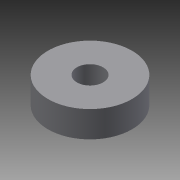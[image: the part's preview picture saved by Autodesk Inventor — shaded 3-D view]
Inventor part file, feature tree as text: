
AUTODESK INVENTOR PART (.ipt)
format: ipt  version: 2013 (Build 170138000, 138)  size: 72,704 bytes
history: native  units: mm
features: extrude x1, sketch x1
ambient origin geometry x8: Origin, YZ Plane, XZ Plane, XY Plane, X Axis, Y Axis, Z Axis, Center Point
bodies: Solid1 (feature_tree)
feature tree (2):
  extrude  "Extrusion1"  Depth=16.0mm
  sketch  "Sketch1"  dims[d0=5.0mm d2=16.0mm d3=5.0mm d4=0.0mm]
